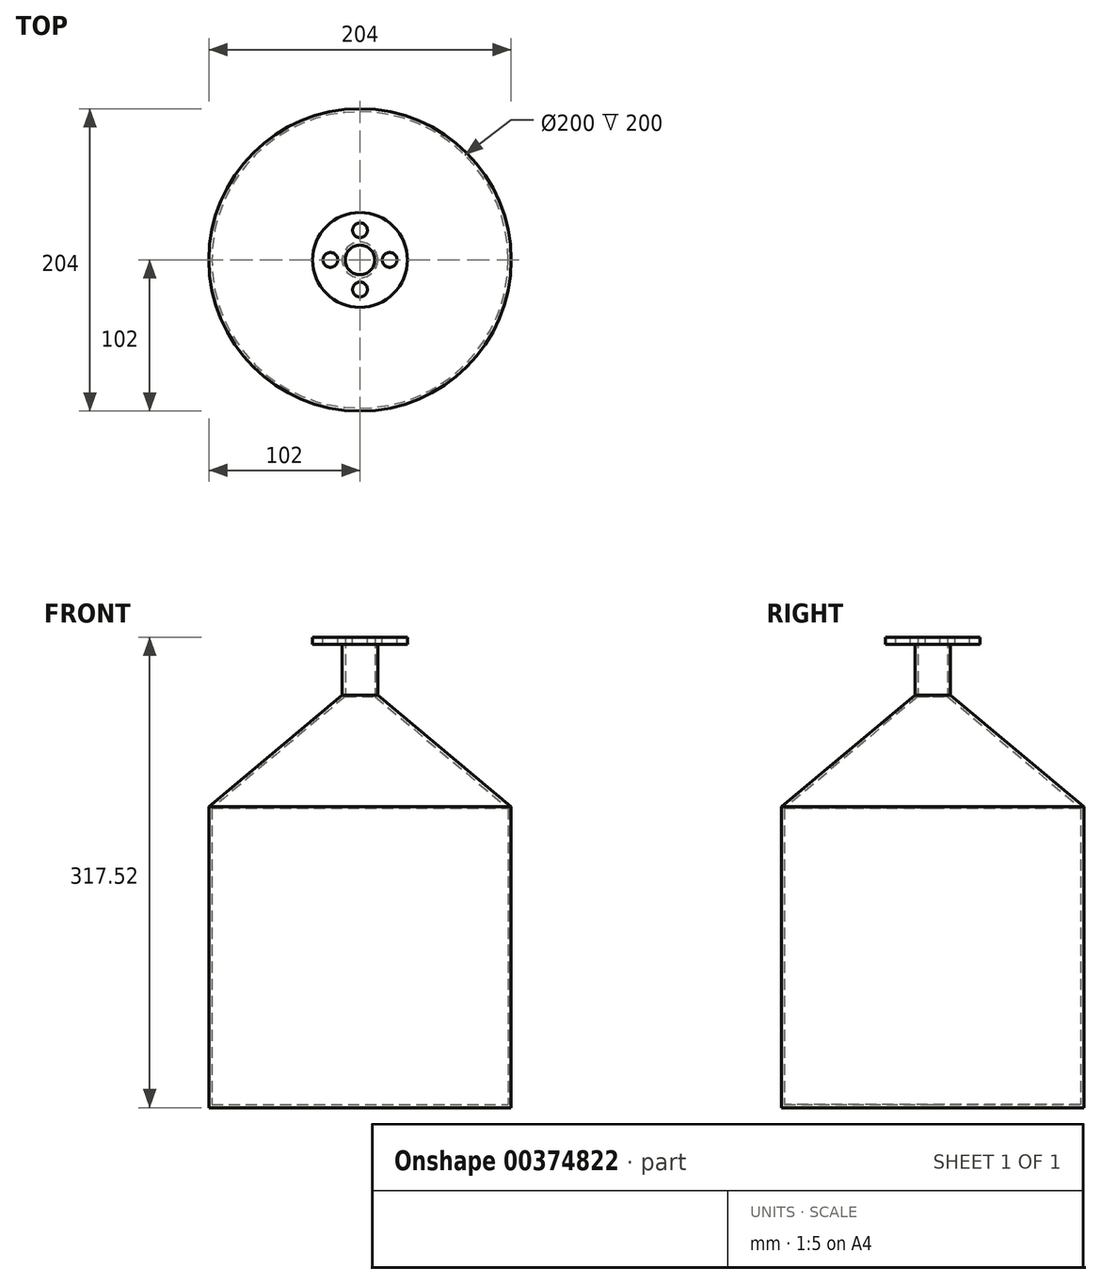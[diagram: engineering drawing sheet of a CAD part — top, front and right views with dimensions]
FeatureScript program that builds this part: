
annotation { "Feature Type Name" : "Feature", "Feature Type Description" : "" }
export const myFeature = defineFeature(function(context is Context, id is Id, definition is map)
    precondition{}
    {
        {
            var Q0;
            Q0=qCreatedBy(makeId("Front.planeOp"),FACE);
            var sketch = newSketch(context, id + "F0", { "sketchPlane" : qUnion([Q0])});
            skLineSegment(sketch, "E0", {"start": v(-100, 200) * mm, "end": v(-100, 0) * mm});
            skLineSegment(sketch, "E1", {"start": v(-100, 0) * mm, "end": v(0, 0) * mm});
            skLineSegment(sketch, "E2", {"start": v(0, 0) * mm, "end": v(0, 240) * mm, "construction": true});
            skLineSegment(sketch, "E3", {"start": v(0, 0) * mm, "end": v(0, -2) * mm});
            skLineSegment(sketch, "E4", {"start": v(-100, 200) * mm, "end": v(-10, 275.52) * mm});
            skPoint(sketch, "E5.start.orphan", {"position": v(-10, 311.04) * mm});
            skPoint(sketch, "E6.start.orphan", {"position": v(-10, 240) * mm});
            skLineSegment(sketch, "E7", {"start": v(-10, 275.52) * mm, "end": v(-10, 315.52) * mm});
            skLineSegment(sketch, "E8.0", {"start": v(-12, 276.45) * mm, "end": v(-12, 315.52) * mm});
            skLineSegment(sketch, "E8.1", {"start": v(-102, 200.93) * mm, "end": v(-12, 276.45) * mm});
            skLineSegment(sketch, "E8.2", {"start": v(-102, 200.93) * mm, "end": v(-102, -2) * mm});
            skLineSegment(sketch, "E8.3", {"start": v(-102, -2) * mm, "end": v(0, -2) * mm});
            skLineSegment(sketch, "E9", {"start": v(-12, 315.52) * mm, "end": v(-10, 315.52) * mm});
            skSolve(sketch);
        }
        {
            var Q0;
            Q0 = qSketchRegion(id + "F0", true);
            var Q1;
            Q1=sQuery(id+"F0.wireOp",EDGE,"E2");
            revolve(context, id + "F1", {"entities" : qUnion([Q0]), "axis" : qUnion([Q1]), "revolveType" : RevolveType.FULL});
        }
        {
            var Q0;
            Q0=makeQuery(id+"F1.opRevolve","SWEPT_FACE",FACE,{"disambiguationData":[OSD([sQuery(id+"F0.wireOp",EDGE,"E9")])]});
            var sketch = newSketch(context, id + "F2", { "sketchPlane" : qUnion([Q0])});
            skCircle(sketch, "E10", {"center": v(0, 0) * mm, "radius": 32 * mm});
            skSolve(sketch);
        }
        {
            var Q0;
            Q0=makeQuery(id+"F2.imprint","IMPRINT",FACE,{"disambiguationData":[TD([[makeQuery(id+"F2.imprint","IMPRINT",EDGE,{"derivedFrom":sQuery(id+"F2.wireOp",EDGE,"E10")}),1.0]])]});
            extrude(context, id + "F3", {"entities" : qUnion([Q0]), "operationType" : NewBodyOperationType.ADD, "oppositeDirection" : true, "depth" : 5 * mm});
        }
        {
            var Q0;
            {var subQ0=sQuery(id+"F0.wireOp",EDGE,"E9");Q0=makeQuery(id+"F3.boolean.opBoolean","MERGE",FACE,{"derivedFrom":[makeQuery(id+"F1.opRevolve","SWEPT_FACE",FACE,{"disambiguationData":[OSD([subQ0])]}),makeQuery(id+"F3.opExtrude","CAP_FACE",FACE,{"disambiguationData":[OSD([sQuery(id+"F0.wireOp",EDGE,"E8.0"),subQ0,sQuery(id+"F2.wireOp",EDGE,"E10")])],"isStart":true})]});}
            var sketch = newSketch(context, id + "F4", { "sketchPlane" : qUnion([Q0])});
            skCircle(sketch, "E11", {"center": v(0, 20) * mm, "radius": 5 * mm});
            skCircle(sketch, "E12.1.0", {"center": v(-20, 0) * mm, "radius": 5 * mm});
            skCircle(sketch, "E12.2.0", {"center": v(0, -20) * mm, "radius": 5 * mm});
            skPoint(sketch, "E12.center", {"position": v(0, 0) * mm});
            skCircle(sketch, "E13.1.3.0", {"center": v(20, 0) * mm, "radius": 5 * mm});
            skSolve(sketch);
        }
        {
            var Q0;
            Q0 = qSketchRegion(id + "F4", true);
            var Q1;
            Q1=makeQuery(id+"F3.opExtrude","CAP_FACE",FACE,{"disambiguationData":[OSD([sQuery(id+"F0.wireOp",EDGE,"E8.0"),sQuery(id+"F0.wireOp",EDGE,"E9"),sQuery(id+"F2.wireOp",EDGE,"E10")])],"isStart":false});
            extrude(context, id + "F5", {"entities" : qUnion([Q0]), "operationType" : NewBodyOperationType.REMOVE, "endBound" : BoundingType.UP_TO_SURFACE, "oppositeDirection" : true, "endBoundEntityFace" : qUnion([Q1]), "depth" : 25 * mm});
        }
    });
